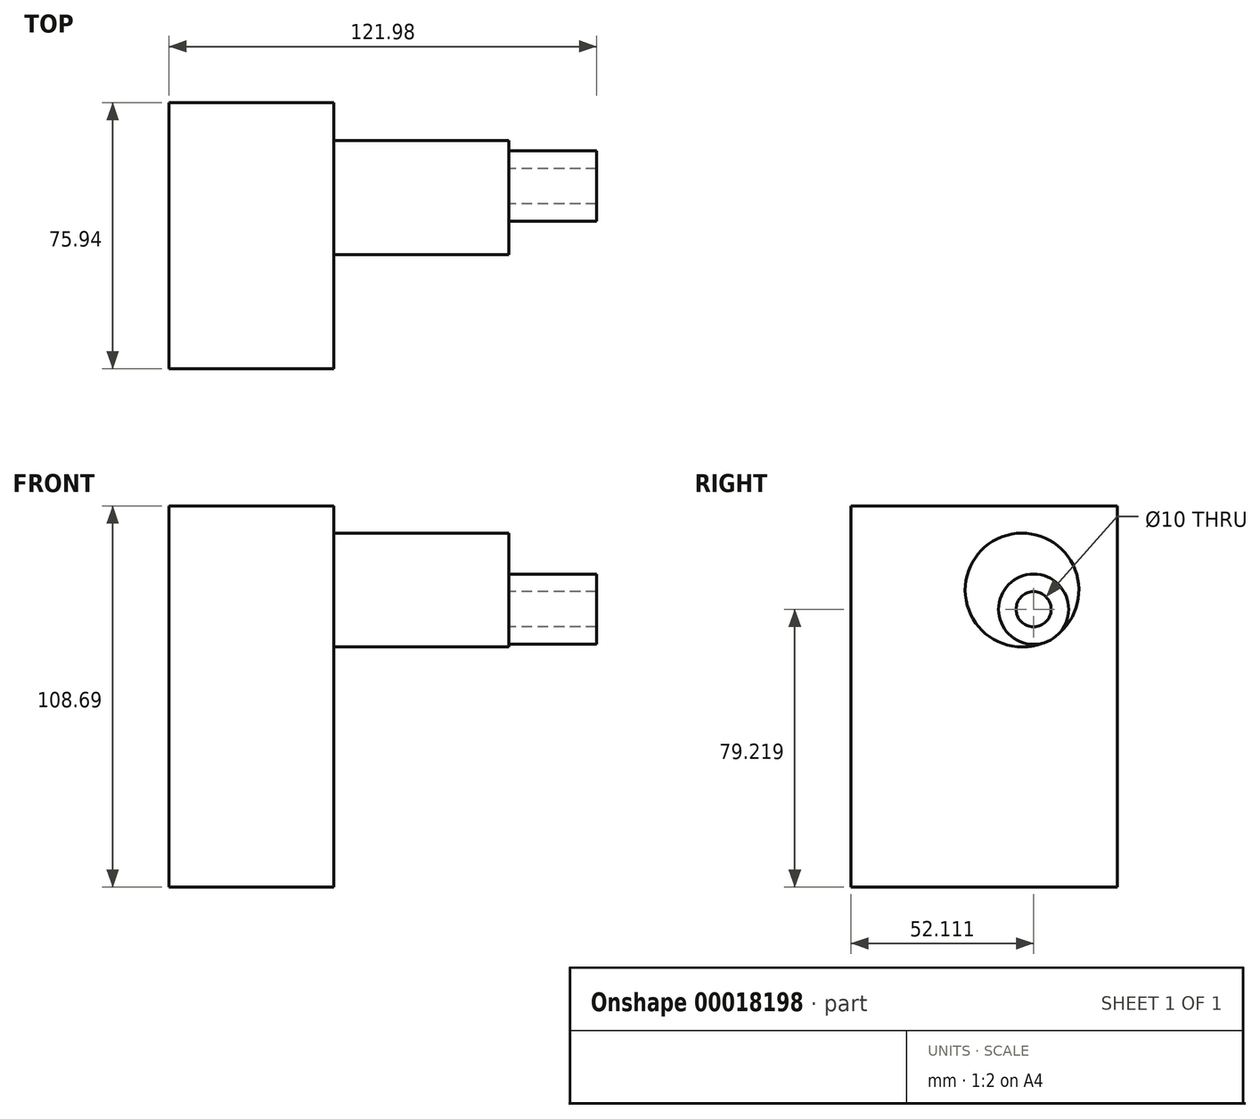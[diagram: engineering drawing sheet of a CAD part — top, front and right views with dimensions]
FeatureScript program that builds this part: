
annotation { "Feature Type Name" : "Feature", "Feature Type Description" : "" }
export const myFeature = defineFeature(function(context is Context, id is Id, definition is map)
    precondition{}
    {
        {
            var Q0;
            Q0=qCreatedBy(makeId("Right.planeOp"),FACE);
            var sketch = newSketch(context, id + "F0", { "sketchPlane" : qUnion([Q0])});
            skLineSegment(sketch, "E0.bottom", {"start": v(-28.66, -42.02) * mm, "end": v(47.28, -42.02) * mm});
            skLineSegment(sketch, "E0.top", {"start": v(-28.66, 66.67) * mm, "end": v(47.28, 66.67) * mm});
            skLineSegment(sketch, "E0.left", {"start": v(-28.66, -42.02) * mm, "end": v(-28.66, 66.67) * mm});
            skLineSegment(sketch, "E0.right", {"start": v(47.28, -42.02) * mm, "end": v(47.28, 66.67) * mm});
            skSolve(sketch);
        }
        {
            var Q0;
            Q0=makeQuery(id+"F0.imprint","IMPRINT",FACE,{"disambiguationData":[TD([[makeQuery(id+"F0.imprint","IMPRINT",EDGE,{"derivedFrom":sQuery(id+"F0.wireOp",EDGE,"E0.bottom")}),1.0]])]});
            extrude(context, id + "F1", {"entities" : qUnion([Q0]), "depth" : 46.98 * mm});
        }
        {
            var Q0;
            Q0=makeQuery(id+"F1.opExtrude","CAP_FACE",FACE,{"disambiguationData":[OSD([sQuery(id+"F0.wireOp",EDGE,"E0.bottom"),sQuery(id+"F0.wireOp",EDGE,"E0.top"),sQuery(id+"F0.wireOp",EDGE,"E0.left"),sQuery(id+"F0.wireOp",EDGE,"E0.right")])],"isStart":false});
            var sketch = newSketch(context, id + "F2", { "sketchPlane" : qUnion([Q0])});
            skSolve(sketch);
        }
        {
            var Q0;
            Q0=makeQuery(id+"F2.imprint","IMPRINT",FACE,{"disambiguationData":[TD([[makeQuery(id+"F2.imprint","IMPRINT",EDGE,{"derivedFrom":makeQuery(id+"F1.opExtrude","CAP_EDGE",EDGE,{"disambiguationData":[OSD([sQuery(id+"F0.wireOp",EDGE,"E0.bottom")])],"isStart":false})}),1.0]])]});
            var sketch = newSketch(context, id + "F3", { "sketchPlane" : qUnion([Q0])});
            skCircle(sketch, "E1", {"center": v(20.15, 42.67) * mm, "radius": 16.21 * mm});
            skSolve(sketch);
        }
        {
            var Q0;
            Q0=makeQuery(id+"F3.imprint","IMPRINT",FACE,{"disambiguationData":[TD([[makeQuery(id+"F3.imprint","IMPRINT",EDGE,{"derivedFrom":sQuery(id+"F3.wireOp",EDGE,"E1")}),1.0]])]});
            var Q1;
            Q1=sQuery(id+"F3.wireOp",EDGE,"E1");
            extrude(context, id + "F4", {"entities" : qUnion([Q0]), "surfaceEntities" : qUnion([Q1]), "depth" : 50 * mm});
        }
        {
            var Q0;
            Q0=makeQuery(id+"F4.opExtrude","CAP_FACE",FACE,{"disambiguationData":[OSD([sQuery(id+"F3.wireOp",EDGE,"E1")])],"isStart":false});
            var sketch = newSketch(context, id + "F5", { "sketchPlane" : qUnion([Q0])});
            skCircle(sketch, "E2", {"center": v(23.45, 37.2) * mm, "radius": 5 * mm});
            skCircle(sketch, "E3.0", {"center": v(23.45, 37.2) * mm, "radius": 10 * mm});
            skSolve(sketch);
        }
        {
            var Q0;
            Q0 = qSketchRegion(id + "F5", true);
            var Q1;
            Q1=sQuery(id+"F5.wireOp",EDGE,"E3.0");
            var Q2;
            Q2=sQuery(id+"F5.wireOp",EDGE,"E2");
            extrude(context, id + "F6", {"entities" : qUnion([Q0]), "surfaceEntities" : qUnion([Q1, Q2]), "depth" : 25 * mm});
        }
    });
